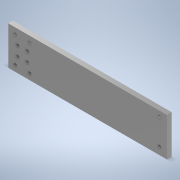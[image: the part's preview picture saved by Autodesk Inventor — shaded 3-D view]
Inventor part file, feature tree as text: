
AUTODESK INVENTOR PART (.ipt)
format: ipt  version: 2020 (Build 240168000, 168)  size: 284,160 bytes
history: native  units: in
note: dims shown in document units (in); Inventor stores cm internally (conversion verified against a paired STEP export)
features: reference x5, extrude x4, sketch x4, other x3
ambient origin geometry x8: Origin, YZ Plane, XZ Plane, XY Plane, X Axis, Y Axis, Z Axis, Center Point
bodies: Solid1 (feature_tree)
feature tree (16):
  extrude  "Extrusion1"  Depth=4.0in
  extrude  "Extrusion3"  Depth=0.3125in
  extrude  "Extrusion4"  Depth=0.5in TaperAngle=0.0deg
  extrude  "Extrusion5"  Depth=0.5in
  sketch  "Sketch1"  dims[d0=3.0in d1=4.0in]
  reference  "Reference1"
  reference  "Reference2"
  reference  "Reference3"
  reference  "Reference4"
  reference  "Reference5"
  sketch  "Sketch3"  dims[d2=0.3125in d3=0.625in]
  sketch  "Sketch4"  dims[d4=0.75in d5=0.5in d6=0.0in]
  sketch  "Sketch5"  dims[d16=1.75in d17=1.75in d18=1.125in d19=0.625in d23=0.5in d24=0.375in d25=0.375in d26=0.7874in d28=1.0in d29=0.7874in d31=1.0in d34=0.3125in d35=0.0in d36=0.3125in d37=0.3125in d38=0.3125in d39=0.3125in d40=0.3125in d41=0.0in d42=0.3125in d43=0.3125in d44=0.75in d45=0.75in d46=0.5in d47=0.0in]
  other  "<userpath>\Desktop\PnP Machine\PnP Machine.iam"
  other  "PnP Machine.iam"
  other  "47065T605_ALUMINUM T-SLOTTED FRAMING EXTRUSION:2"
